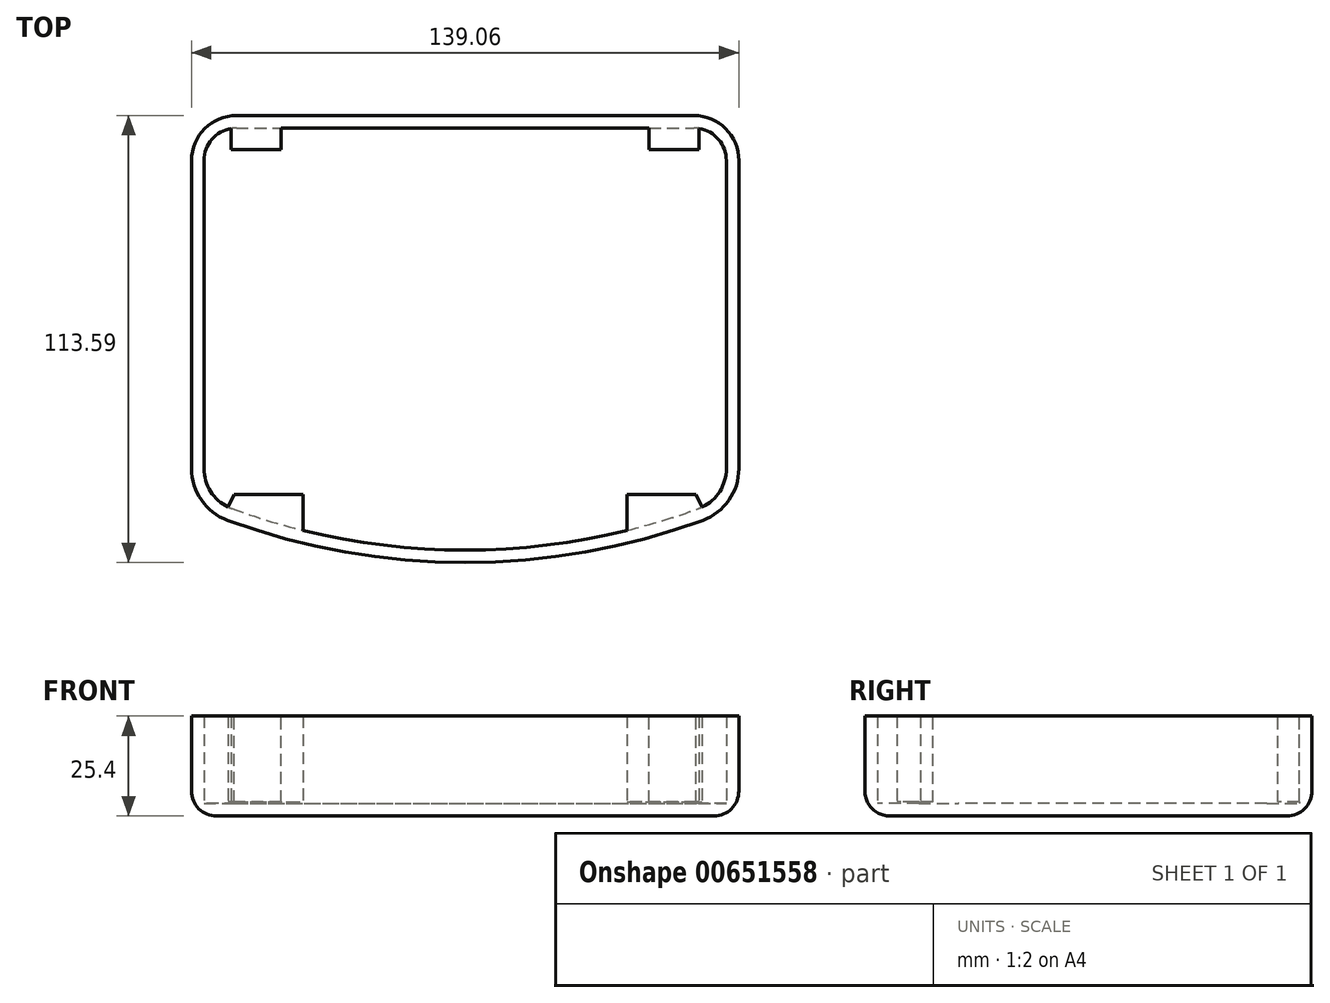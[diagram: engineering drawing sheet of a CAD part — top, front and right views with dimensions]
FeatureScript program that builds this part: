
annotation { "Feature Type Name" : "Feature", "Feature Type Description" : "" }
export const myFeature = defineFeature(function(context is Context, id is Id, definition is map)
    precondition{}
    {
        {
            var Q0;
            Q0=qCreatedBy(makeId("Top.planeOp"),FACE);
            var sketch = newSketch(context, id + "F0", { "sketchPlane" : qUnion([Q0])});
            skLineSegment(sketch, "E0", {"start": v(-58.1, 62.54) * mm, "end": v(58.1, 62.54) * mm});
            skArc(sketch, "E1", {"start": v(-60.37, -40.31) * mm, "mid": v(0, -51.05) * mm, "end": v(60.37, -40.31) * mm});
            skPoint(sketch, "E2", {"position": v(0, -51.05) * mm});
            skLineSegment(sketch, "E3", {"start": v(-69.53, 51.1) * mm, "end": v(-69.53, -27.2) * mm});
            skLineSegment(sketch, "E4.MirrorCS", {"start": v(69.53, 51.1) * mm, "end": v(69.53, -27.2) * mm});
            skPoint(sketch, "E5.orphan", {"position": v(-69.53, -43.52) * mm});
            skPoint(sketch, "E6.orphan", {"position": v(69.53, -43.52) * mm});
            skPoint(sketch, "E7.visualSharp", {"position": v(-69.53, 62.54) * mm});
            skArc(sketch, "E7.filletArc", {"start": v(-58.1, 62.54) * mm, "mid": v(-66.18, 59.19) * mm, "end": v(-69.53, 51.1) * mm});
            skPoint(sketch, "E8.visualSharp", {"position": v(69.53, 62.54) * mm});
            skArc(sketch, "E8.filletArc", {"start": v(69.53, 51.1) * mm, "mid": v(66.18, 59.19) * mm, "end": v(58.1, 62.54) * mm});
            skPoint(sketch, "E9.visualSharp", {"position": v(-69.53, -36.66) * mm});
            skArc(sketch, "E9.filletArc", {"start": v(-69.53, -27.2) * mm, "mid": v(-67.01, -35.2) * mm, "end": v(-60.37, -40.31) * mm});
            skPoint(sketch, "E10.visualSharp", {"position": v(69.53, -36.66) * mm});
            skArc(sketch, "E10.filletArc", {"start": v(60.37, -40.31) * mm, "mid": v(67.01, -35.2) * mm, "end": v(69.53, -27.2) * mm});
            skSolve(sketch);
        }
        {
            var Q0;
            Q0=makeQuery(id+"F0.imprint","IMPRINT",FACE,{"disambiguationData":[TD([[makeQuery(id+"F0.imprint","IMPRINT",EDGE,{"derivedFrom":sQuery(id+"F0.wireOp",EDGE,"E0")}),-1.0]])]});
            extrude(context, id + "F1", {"entities" : qUnion([Q0]), "depth" : 25.4 * mm, "offsetDistance" : 25.4 * mm});
        }
        {
            var Q0;
            Q0=makeQuery(id+"F1.opExtrude","CAP_FACE",FACE,{"disambiguationData":[OSD([sQuery(id+"F0.wireOp",EDGE,"E0"),sQuery(id+"F0.wireOp",EDGE,"E1"),sQuery(id+"F0.wireOp",EDGE,"E3"),sQuery(id+"F0.wireOp",EDGE,"E4.MirrorCS"),sQuery(id+"F0.wireOp",EDGE,"E7.filletArc"),sQuery(id+"F0.wireOp",EDGE,"E8.filletArc"),sQuery(id+"F0.wireOp",EDGE,"E9.filletArc"),sQuery(id+"F0.wireOp",EDGE,"E10.filletArc")])],"isStart":false});
            shell(context, id + "F2", {"entities" : qUnion([Q0]), "thickness" : 3.17 * mm});
        }
        {
            var Q0;
            Q0=makeQuery(id+"F1.opExtrude","CAP_FACE",FACE,{"disambiguationData":[OSD([sQuery(id+"F0.wireOp",EDGE,"E0"),sQuery(id+"F0.wireOp",EDGE,"E1"),sQuery(id+"F0.wireOp",EDGE,"E3"),sQuery(id+"F0.wireOp",EDGE,"E4.MirrorCS"),sQuery(id+"F0.wireOp",EDGE,"E7.filletArc"),sQuery(id+"F0.wireOp",EDGE,"E8.filletArc"),sQuery(id+"F0.wireOp",EDGE,"E9.filletArc"),sQuery(id+"F0.wireOp",EDGE,"E10.filletArc")])],"isStart":true});
            fillet(context, id + "F3", {"entities" : qUnion([Q0]), "radius" : 6.35 * mm, "tangentPropagation" : true, "allowEdgeOverflow" : false});
        }
        {
            var Q0;
            Q0=qCreatedBy(makeId("Top.planeOp"),FACE);
            cPlane(context, id + "F4", {"entities" : qUnion([Q0]), "cplaneType" : CPlaneType.OFFSET, "offset" : 25.4 * mm, "width" : 152.4 * mm, "height" : 152.4 * mm});
        }
        {
            var Q0;
            Q0=qCreatedBy(id+"F4.planeOp",FACE);
            var sketch = newSketch(context, id + "F5", { "sketchPlane" : qUnion([Q0])});
            skLineSegment(sketch, "E11.MirrorCS", {"start": v(46.73, 60.26) * mm, "end": v(46.73, 53.9) * mm});
            skLineSegment(sketch, "E12.MirrorCS", {"start": v(46.73, 60.26) * mm, "end": v(59.43, 60.26) * mm});
            skLineSegment(sketch, "E13.MirrorCS", {"start": v(46.73, 53.9) * mm, "end": v(59.43, 53.9) * mm});
            skLineSegment(sketch, "E14.MirrorCS", {"start": v(59.43, 60.26) * mm, "end": v(59.43, 53.9) * mm});
            skLineSegment(sketch, "E15", {"start": v(-58.7, -33.77) * mm, "end": v(-60.64, -37.91) * mm});
            skLineSegment(sketch, "E16", {"start": v(-60.64, -37.91) * mm, "end": v(-53.9, -40.27) * mm});
            skLineSegment(sketch, "E17.MirrorCS", {"start": v(58.7, -33.77) * mm, "end": v(60.64, -37.91) * mm});
            skLineSegment(sketch, "E18.MirrorCS", {"start": v(60.64, -37.91) * mm, "end": v(53.9, -40.27) * mm});
            skLineSegment(sketch, "E19.MirrorCS", {"start": v(-59.43, 60.26) * mm, "end": v(-59.43, 53.9) * mm});
            skLineSegment(sketch, "E20.MirrorCS", {"start": v(-46.73, 53.9) * mm, "end": v(-59.43, 53.9) * mm});
            skLineSegment(sketch, "E21.MirrorCS", {"start": v(-46.73, 60.26) * mm, "end": v(-46.73, 53.9) * mm});
            skLineSegment(sketch, "E22.MirrorCS", {"start": v(-46.73, 60.26) * mm, "end": v(-59.43, 60.26) * mm});
            skLineSegment(sketch, "E23", {"start": v(-58.7, -33.77) * mm, "end": v(-41.16, -33.77) * mm});
            skLineSegment(sketch, "E24", {"start": v(-41.16, -33.77) * mm, "end": v(-41.16, -43.82) * mm});
            skLineSegment(sketch, "E25", {"start": v(-41.16, -43.82) * mm, "end": v(-53.9, -40.27) * mm});
            skLineSegment(sketch, "E26.MirrorCS", {"start": v(58.7, -33.77) * mm, "end": v(41.16, -33.77) * mm});
            skLineSegment(sketch, "E27.MirrorCS", {"start": v(41.16, -33.77) * mm, "end": v(41.16, -43.82) * mm});
            skLineSegment(sketch, "E28.MirrorCS", {"start": v(41.16, -43.82) * mm, "end": v(53.9, -40.27) * mm});
            skSolve(sketch);
        }
        {
            var Q0;
            Q0=makeQuery(id+"F5.imprint","IMPRINT",FACE,{"disambiguationData":[TD([[makeQuery(id+"F5.imprint","IMPRINT",EDGE,{"derivedFrom":sQuery(id+"F5.wireOp",EDGE,"E19.MirrorCS")}),1.0]])]});
            var Q1;
            Q1=makeQuery(id+"F5.imprint","IMPRINT",FACE,{"disambiguationData":[TD([[makeQuery(id+"F5.imprint","IMPRINT",EDGE,{"derivedFrom":sQuery(id+"F5.wireOp",EDGE,"9519add0-a8e1-4df8-8314-173779524e8a")}),1.0]])]});
            var Q2;
            Q2=makeQuery(id+"F5.imprint","IMPRINT",FACE,{"disambiguationData":[TD([[makeQuery(id+"F5.imprint","IMPRINT",EDGE,{"derivedFrom":sQuery(id+"F5.wireOp",EDGE,"E11.MirrorCS")}),1.0]])]});
            var Q3;
            Q3=makeQuery(id+"F5.imprint","IMPRINT",FACE,{"disambiguationData":[TD([[makeQuery(id+"F5.imprint","IMPRINT",EDGE,{"derivedFrom":sQuery(id+"F5.wireOp",EDGE,"307c7df9-c839-4614-8c11-209d964d54c6.MirrorCS")}),-1.0]])]});
            var Q4;
            Q4=makeQuery(id+"F5.imprint","IMPRINT",FACE,{"disambiguationData":[TD([[makeQuery(id+"F5.imprint","IMPRINT",EDGE,{"derivedFrom":sQuery(id+"F5.wireOp",EDGE,"E15")}),1.0]])]});
            var Q5;
            Q5=makeQuery(id+"F5.imprint","IMPRINT",FACE,{"disambiguationData":[TD([[makeQuery(id+"F5.imprint","IMPRINT",EDGE,{"derivedFrom":sQuery(id+"F5.wireOp",EDGE,"E17.MirrorCS")}),-1.0]])]});
            extrude(context, id + "F6", {"entities" : qUnion([Q0, Q1, Q2, Q3, Q4, Q5]), "operationType" : NewBodyOperationType.ADD, "oppositeDirection" : true, "depth" : 21.84 * mm, "offsetDistance" : 25.4 * mm});
        }
    });
